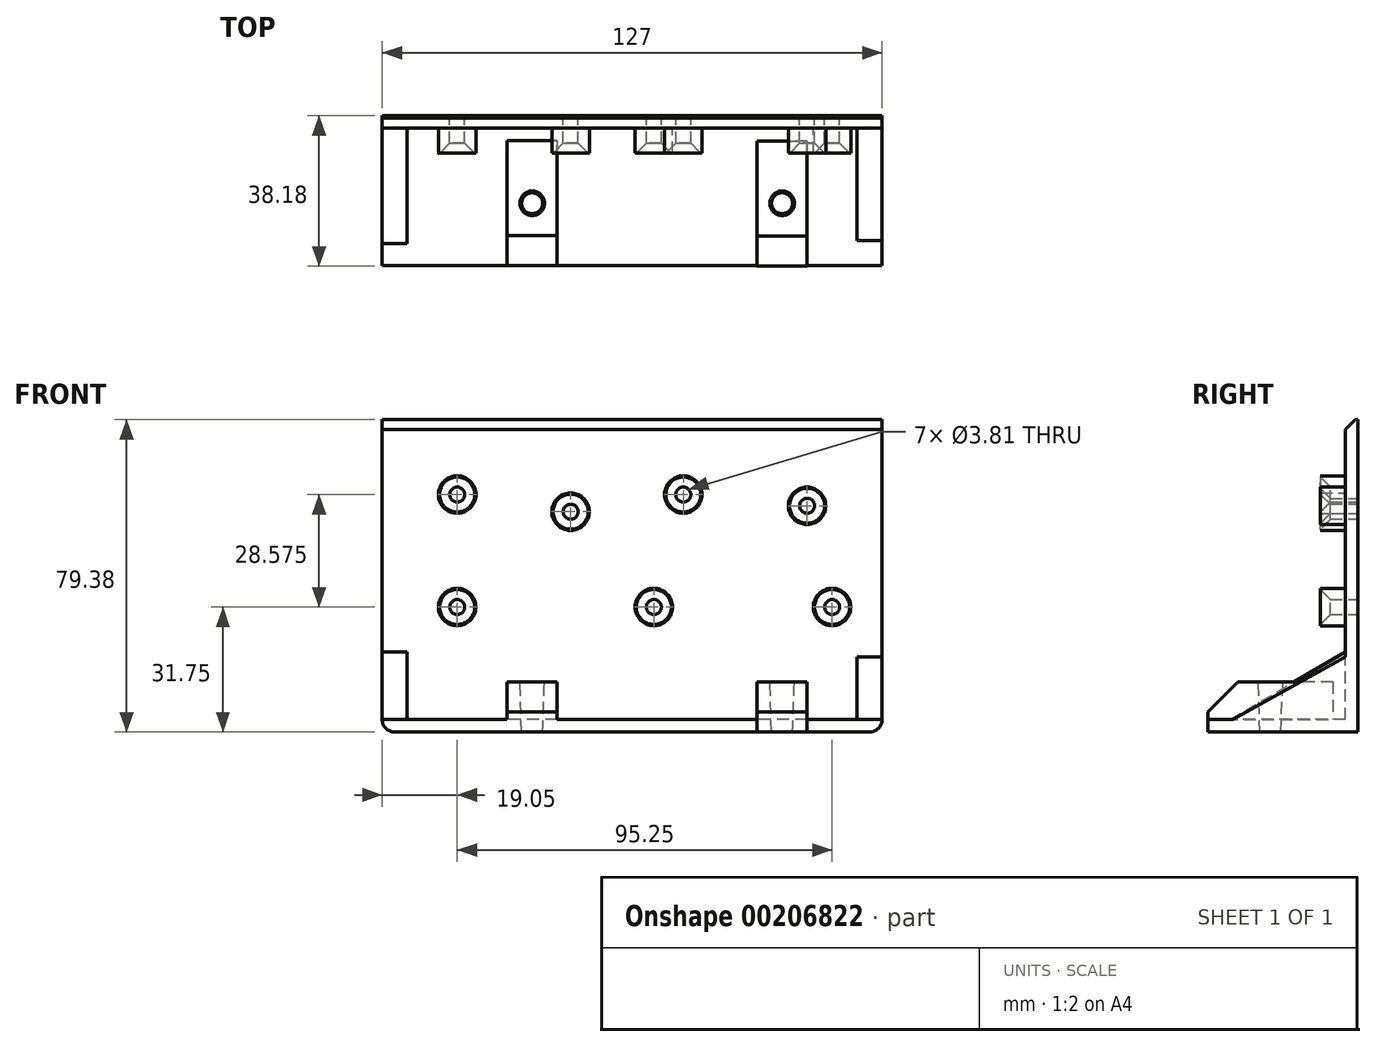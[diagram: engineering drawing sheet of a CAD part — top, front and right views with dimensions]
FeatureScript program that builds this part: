
annotation { "Feature Type Name" : "Feature", "Feature Type Description" : "" }
export const myFeature = defineFeature(function(context is Context, id is Id, definition is map)
    precondition{}
    {
        {
            var Q0;
            Q0=qCreatedBy(makeId("Top.planeOp"),FACE);
            var sketch = newSketch(context, id + "F0", { "sketchPlane" : qUnion([Q0])});
            skLineSegment(sketch, "E0", {"start": v(110.05, 0) * mm, "end": v(-130.25, 0) * mm, "construction": true});
            skLineSegment(sketch, "E1", {"start": v(0, 83.53) * mm, "end": v(0, -84.25) * mm, "construction": true});
            skSolve(sketch);
        }
        {
            var Q0;
            Q0=qCreatedBy(makeId("Top.planeOp"),FACE);
            var sketch = newSketch(context, id + "F1", { "sketchPlane" : qUnion([Q0])});
            skLineSegment(sketch, "E2.bottom", {"start": v(0, 0) * mm, "end": v(127, 0) * mm});
            skLineSegment(sketch, "E2.top", {"start": v(0, -38.1) * mm, "end": v(127, -38.1) * mm});
            skLineSegment(sketch, "E2.left", {"start": v(0, 0) * mm, "end": v(0, -38.1) * mm});
            skLineSegment(sketch, "E2.right", {"start": v(127, 0) * mm, "end": v(127, -38.1) * mm});
            skSolve(sketch);
        }
        {
            var Q0;
            Q0=makeQuery(id+"F1.imprint","IMPRINT",FACE,{"disambiguationData":[TD([[makeQuery(id+"F1.imprint","IMPRINT",EDGE,{"derivedFrom":sQuery(id+"F1.wireOp",EDGE,"E2.bottom")}),-1.0]])]});
            extrude(context, id + "F2", {"entities" : qUnion([Q0]), "depth" : 3.17 * mm});
        }
        {
            var Q0;
            Q0=qCreatedBy(makeId("Front.planeOp"),FACE);
            var sketch = newSketch(context, id + "F3", { "sketchPlane" : qUnion([Q0])});
            skLineSegment(sketch, "E3", {"start": v(0, -41.27) * mm, "end": v(0, 86.17) * mm, "construction": true});
            skSolve(sketch);
        }
        {
            var Q0;
            Q0=makeQuery(id+"F2.opExtrude","CAP_FACE",FACE,{"disambiguationData":[OSD([sQuery(id+"F1.wireOp",EDGE,"E2.bottom"),sQuery(id+"F1.wireOp",EDGE,"E2.top"),sQuery(id+"F1.wireOp",EDGE,"E2.left"),sQuery(id+"F1.wireOp",EDGE,"E2.right")])],"isStart":false});
            var sketch = newSketch(context, id + "F4", { "sketchPlane" : qUnion([Q0])});
            skLineSegment(sketch, "E4.bottom", {"start": v(0, 0) * mm, "end": v(127, 0) * mm});
            skLineSegment(sketch, "E4.top", {"start": v(0, -3.18) * mm, "end": v(127, -3.18) * mm});
            skLineSegment(sketch, "E4.left", {"start": v(0, 0) * mm, "end": v(0, -3.18) * mm});
            skLineSegment(sketch, "E4.right", {"start": v(127, 0) * mm, "end": v(127, -3.18) * mm});
            skSolve(sketch);
        }
        {
            var Q0;
            Q0=makeQuery(id+"F4.imprint","IMPRINT",FACE,{"disambiguationData":[TD([[makeQuery(id+"F4.imprint","IMPRINT",EDGE,{"derivedFrom":sQuery(id+"F4.wireOp",EDGE,"E4.bottom")}),-1.0]])]});
            extrude(context, id + "F5", {"entities" : qUnion([Q0]), "operationType" : NewBodyOperationType.ADD, "depth" : 76.2 * mm});
        }
        {
            var Q0;
            Q0=qCreatedBy(makeId("Top.planeOp"),FACE);
            var sketch = newSketch(context, id + "F6", { "sketchPlane" : qUnion([Q0])});
            skCircle(sketch, "E5", {"center": v(38.1, -22.23) * mm, "radius": 2.67 * mm});
            skCircle(sketch, "E6", {"center": v(101.6, -22.23) * mm, "radius": 2.67 * mm});
            skSolve(sketch);
        }
        {
            var Q0;
            Q0=qCreatedBy(makeId("Top.planeOp"),FACE);
            var sketch = newSketch(context, id + "F7", { "sketchPlane" : qUnion([Q0])});
            skLineSegment(sketch, "E7.bottom", {"start": v(31.75, -6.35) * mm, "end": v(44.45, -6.35) * mm});
            skLineSegment(sketch, "E7.top", {"start": v(31.75, -38.1) * mm, "end": v(44.45, -38.1) * mm});
            skLineSegment(sketch, "E7.left", {"start": v(31.75, -6.35) * mm, "end": v(31.75, -38.1) * mm});
            skLineSegment(sketch, "E7.right", {"start": v(44.45, -6.35) * mm, "end": v(44.45, -38.1) * mm});
            skLineSegment(sketch, "E8.bottom", {"start": v(95.25, -6.43) * mm, "end": v(107.95, -6.43) * mm});
            skLineSegment(sketch, "E8.top", {"start": v(95.25, -38.18) * mm, "end": v(107.95, -38.18) * mm});
            skLineSegment(sketch, "E8.left", {"start": v(95.25, -6.43) * mm, "end": v(95.25, -38.18) * mm});
            skLineSegment(sketch, "E8.right", {"start": v(107.95, -6.43) * mm, "end": v(107.95, -38.18) * mm});
            skSolve(sketch);
        }
        {
            var Q0;
            Q0 = qSketchRegion(id + "F7", true);
            extrude(context, id + "F8", {"entities" : qUnion([Q0]), "operationType" : NewBodyOperationType.ADD, "depth" : 12.7 * mm});
        }
        {
            var Q0;
            Q0=makeQuery(id+"F6.imprint","IMPRINT",FACE,{"disambiguationData":[TD([[makeQuery(id+"F6.imprint","IMPRINT",EDGE,{"derivedFrom":sQuery(id+"F6.wireOp",EDGE,"E5")}),1.0]])]});
            var Q1;
            Q1=makeQuery(id+"F6.imprint","IMPRINT",FACE,{"disambiguationData":[TD([[makeQuery(id+"F6.imprint","IMPRINT",EDGE,{"derivedFrom":sQuery(id+"F6.wireOp",EDGE,"E6")}),1.0]])]});
            extrude(context, id + "F9", {"entities" : qUnion([Q0, Q1]), "operationType" : NewBodyOperationType.REMOVE, "depth" : 25.4 * mm, "hasDraft" : true, "draftAngle" : 2 * degree});
        }
        {
            var Q0;
            Q0=makeQuery(id+"F2.opExtrude","CAP_EDGE",EDGE,{"disambiguationData":[OSD([sQuery(id+"F1.wireOp",EDGE,"E2.left")])],"isStart":true});
            var Q1;
            Q1=makeQuery(id+"F2.opExtrude","CAP_EDGE",EDGE,{"disambiguationData":[OSD([sQuery(id+"F1.wireOp",EDGE,"E2.right")])],"isStart":true});
            fillet(context, id + "F10", {"entities" : qUnion([Q0, Q1]), "radius" : 3.17 * mm, "tangentPropagation" : true, "allowEdgeOverflow" : false});
        }
        {
            var Q0;
            Q0=makeQuery(id+"F5.boolean.opBoolean","MERGE",FACE,{"derivedFrom":[makeQuery(id+"F2.opExtrude","SWEPT_FACE",FACE,{"disambiguationData":[OSD([sQuery(id+"F1.wireOp",EDGE,"E2.left")])]}),makeQuery(id+"F5.opExtrude","SWEPT_FACE",FACE,{"disambiguationData":[OSD([sQuery(id+"F4.wireOp",EDGE,"E4.left")])]})]});
            var sketch = newSketch(context, id + "F11", { "sketchPlane" : qUnion([Q0])});
            skLineSegment(sketch, "E9", {"start": v(0, 22.22) * mm, "end": v(0, 3.17) * mm});
            skLineSegment(sketch, "E10", {"start": v(0, 3.17) * mm, "end": v(32.45, 3.17) * mm});
            skLineSegment(sketch, "E11", {"start": v(32.45, 3.17) * mm, "end": v(0, 22.22) * mm});
            skSolve(sketch);
        }
        {
            var Q0;
            Q0 = qSketchRegion(id + "F11", true);
            extrude(context, id + "F12", {"entities" : qUnion([Q0]), "operationType" : NewBodyOperationType.ADD, "oppositeDirection" : true, "depth" : 6.35 * mm});
        }
        {
            var Q0;
            Q0=makeQuery(id+"F5.boolean.opBoolean","MERGE",FACE,{"derivedFrom":[makeQuery(id+"F2.opExtrude","SWEPT_FACE",FACE,{"disambiguationData":[OSD([sQuery(id+"F1.wireOp",EDGE,"E2.right")])]}),makeQuery(id+"F5.opExtrude","SWEPT_FACE",FACE,{"disambiguationData":[OSD([sQuery(id+"F4.wireOp",EDGE,"E4.right")])]})]});
            var sketch = newSketch(context, id + "F13", { "sketchPlane" : qUnion([Q0])});
            skLineSegment(sketch, "E12", {"start": v(0, 20.9) * mm, "end": v(0, 3.18) * mm});
            skLineSegment(sketch, "E13", {"start": v(0, 3.17) * mm, "end": v(-31.75, 3.17) * mm});
            skLineSegment(sketch, "E14", {"start": v(-31.75, 3.17) * mm, "end": v(0, 20.9) * mm});
            skSolve(sketch);
        }
        {
            var Q0;
            Q0 = qSketchRegion(id + "F13", true);
            extrude(context, id + "F14", {"entities" : qUnion([Q0]), "operationType" : NewBodyOperationType.ADD, "oppositeDirection" : true, "depth" : 6.35 * mm});
        }
        {
            var Q0;
            Q0=makeQuery(id+"F5.opExtrude","SWEPT_FACE",FACE,{"disambiguationData":[OSD([sQuery(id+"F4.wireOp",EDGE,"E4.top")])]});
            var sketch = newSketch(context, id + "F15", { "sketchPlane" : qUnion([Q0])});
            skCircle(sketch, "E15", {"center": v(19.05, 60.33) * mm, "radius": 4.76 * mm});
            skCircle(sketch, "E16", {"center": v(47.86, 55.97) * mm, "radius": 4.76 * mm});
            skCircle(sketch, "E17", {"center": v(76.49, 60.33) * mm, "radius": 4.76 * mm});
            skCircle(sketch, "E18", {"center": v(107.93, 57.47) * mm, "radius": 4.76 * mm});
            skCircle(sketch, "E19", {"center": v(19.03, 31.75) * mm, "radius": 4.76 * mm});
            skCircle(sketch, "E20", {"center": v(69, 31.75) * mm, "radius": 4.76 * mm});
            skCircle(sketch, "E21", {"center": v(114.28, 31.75) * mm, "radius": 4.76 * mm});
            skLineSegment(sketch, "E22", {"start": v(-5.73, 31.75) * mm, "end": v(121.27, 31.75) * mm, "construction": true});
            skSolve(sketch);
        }
        {
            var Q0;
            Q0 = qSketchRegion(id + "F15", true);
            extrude(context, id + "F16", {"entities" : qUnion([Q0]), "operationType" : NewBodyOperationType.ADD, "depth" : 6.35 * mm});
        }
        {
            var Q0;
            Q0=qCreatedBy(makeId("Front.planeOp"),FACE);
            var sketch = newSketch(context, id + "F17", { "sketchPlane" : qUnion([Q0])});
            skCircle(sketch, "E23", {"center": v(19.05, 60.33) * mm, "radius": 1.9 * mm});
            skCircle(sketch, "E24", {"center": v(47.88, 55.97) * mm, "radius": 1.9 * mm});
            skCircle(sketch, "E25", {"center": v(76.5, 60.33) * mm, "radius": 1.9 * mm});
            skCircle(sketch, "E26", {"center": v(107.95, 57.47) * mm, "radius": 1.9 * mm});
            skCircle(sketch, "E27", {"center": v(19.05, 31.75) * mm, "radius": 1.9 * mm});
            skCircle(sketch, "E28", {"center": v(69.02, 31.75) * mm, "radius": 1.9 * mm});
            skCircle(sketch, "E29", {"center": v(114.3, 31.75) * mm, "radius": 1.9 * mm});
            skLineSegment(sketch, "E30", {"start": v(-5.71, 31.75) * mm, "end": v(121.29, 31.75) * mm, "construction": true});
            skSolve(sketch);
        }
        {
            var Q0;
            Q0 = qSketchRegion(id + "F17", true);
            extrude(context, id + "F18", {"entities" : qUnion([Q0]), "operationType" : NewBodyOperationType.REMOVE, "depth" : 25.4 * mm});
        }
        {
            var Q0;
            Q0=makeQuery(id+"F18.boolean.opBoolean","INTERSECT",EDGE,{"derivedFrom":[makeQuery(id+"F16.opExtrude","CAP_FACE",FACE,{"disambiguationData":[OSD([sQuery(id+"F15.wireOp",EDGE,"E15")])],"isStart":false}),makeQuery(id+"F18.opExtrude","SWEPT_FACE",FACE,{"disambiguationData":[OSD([sQuery(id+"F17.wireOp",EDGE,"E23")])]})]});
            var Q1;
            Q1=makeQuery(id+"F18.boolean.opBoolean","INTERSECT",EDGE,{"derivedFrom":[makeQuery(id+"F16.opExtrude","CAP_FACE",FACE,{"disambiguationData":[OSD([sQuery(id+"F15.wireOp",EDGE,"E16")])],"isStart":false}),makeQuery(id+"F18.opExtrude","SWEPT_FACE",FACE,{"disambiguationData":[OSD([sQuery(id+"F17.wireOp",EDGE,"E24")])]})]});
            var Q2;
            Q2=makeQuery(id+"F18.boolean.opBoolean","INTERSECT",EDGE,{"derivedFrom":[makeQuery(id+"F16.opExtrude","CAP_FACE",FACE,{"disambiguationData":[OSD([sQuery(id+"F15.wireOp",EDGE,"E17")])],"isStart":false}),makeQuery(id+"F18.opExtrude","SWEPT_FACE",FACE,{"disambiguationData":[OSD([sQuery(id+"F17.wireOp",EDGE,"E25")])]})]});
            var Q3;
            Q3=makeQuery(id+"F18.boolean.opBoolean","INTERSECT",EDGE,{"derivedFrom":[makeQuery(id+"F16.opExtrude","CAP_FACE",FACE,{"disambiguationData":[OSD([sQuery(id+"F15.wireOp",EDGE,"E19")])],"isStart":false}),makeQuery(id+"F18.opExtrude","SWEPT_FACE",FACE,{"disambiguationData":[OSD([sQuery(id+"F17.wireOp",EDGE,"E27")])]})]});
            var Q4;
            Q4=makeQuery(id+"F18.boolean.opBoolean","INTERSECT",EDGE,{"derivedFrom":[makeQuery(id+"F16.opExtrude","CAP_FACE",FACE,{"disambiguationData":[OSD([sQuery(id+"F15.wireOp",EDGE,"E18")])],"isStart":false}),makeQuery(id+"F18.opExtrude","SWEPT_FACE",FACE,{"disambiguationData":[OSD([sQuery(id+"F17.wireOp",EDGE,"E26")])]})]});
            var Q5;
            Q5=makeQuery(id+"F18.boolean.opBoolean","INTERSECT",EDGE,{"derivedFrom":[makeQuery(id+"F16.opExtrude","CAP_FACE",FACE,{"disambiguationData":[OSD([sQuery(id+"F15.wireOp",EDGE,"E21")])],"isStart":false}),makeQuery(id+"F18.opExtrude","SWEPT_FACE",FACE,{"disambiguationData":[OSD([sQuery(id+"F17.wireOp",EDGE,"E29")])]})]});
            var Q6;
            Q6=makeQuery(id+"F18.boolean.opBoolean","INTERSECT",EDGE,{"derivedFrom":[makeQuery(id+"F16.opExtrude","CAP_FACE",FACE,{"disambiguationData":[OSD([sQuery(id+"F15.wireOp",EDGE,"E20")])],"isStart":false}),makeQuery(id+"F18.opExtrude","SWEPT_FACE",FACE,{"disambiguationData":[OSD([sQuery(id+"F17.wireOp",EDGE,"E28")])]})]});
            chamfer(context, id + "F19", {"entities" : qUnion([Q0, Q1, Q2, Q3, Q4, Q5, Q6]), "width" : 2.54 * mm, "tangentPropagation" : true});
        }
        {
            var Q0;
            Q0=makeQuery(id+"F5.opExtrude","CAP_EDGE",EDGE,{"disambiguationData":[OSD([sQuery(id+"F4.wireOp",EDGE,"E4.top")])],"isStart":false});
            chamfer(context, id + "F20", {"entities" : qUnion([Q0]), "width" : 2.54 * mm, "tangentPropagation" : true});
        }
        {
            var Q0;
            Q0=makeQuery(id+"F8.opExtrude","CAP_EDGE",EDGE,{"disambiguationData":[OSD([sQuery(id+"F7.wireOp",EDGE,"E7.top")])],"isStart":false});
            var Q1;
            Q1=makeQuery(id+"F8.opExtrude","CAP_EDGE",EDGE,{"disambiguationData":[OSD([sQuery(id+"F7.wireOp",EDGE,"E8.top")])],"isStart":false});
            chamfer(context, id + "F21", {"entities" : qUnion([Q0, Q1]), "width" : 7.62 * mm, "tangentPropagation" : true});
        }
    });
